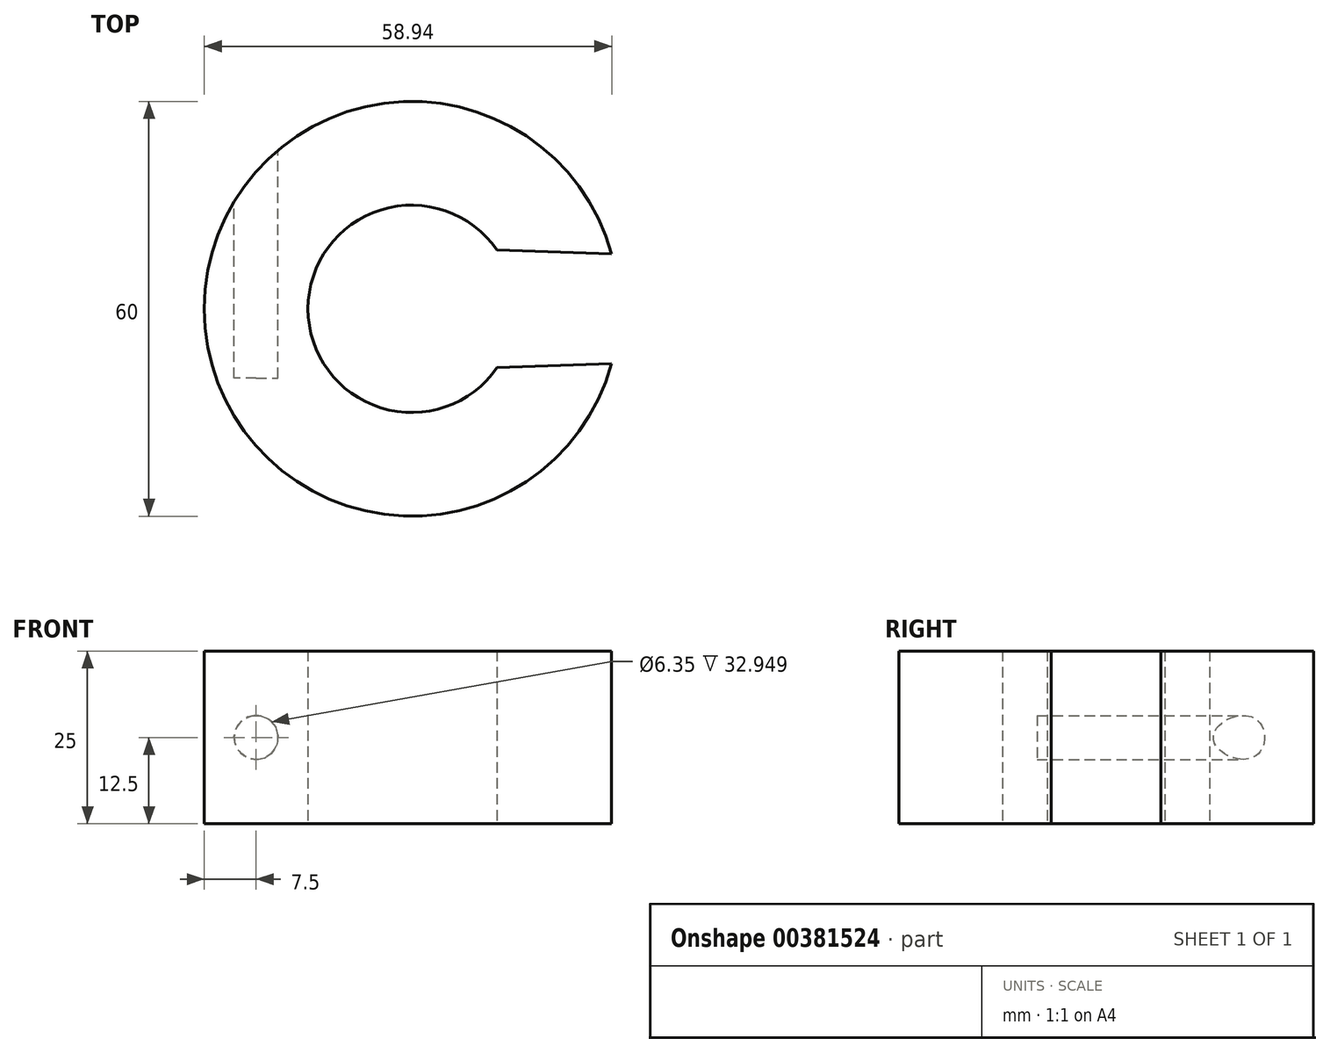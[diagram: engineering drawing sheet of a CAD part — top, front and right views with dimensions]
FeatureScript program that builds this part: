
annotation { "Feature Type Name" : "Feature", "Feature Type Description" : "" }
export const myFeature = defineFeature(function(context is Context, id is Id, definition is map)
    precondition{}
    {
        {
            var Q0;
            Q0=qCreatedBy(makeId("Top.planeOp"),FACE);
            var sketch = newSketch(context, id + "F0", { "sketchPlane" : qUnion([Q0])});
            skArc(sketch, "E0", {"start": v(12.36, 8.5) * mm, "mid": v(-15, 0) * mm, "end": v(12.36, -8.5) * mm});
            skArc(sketch, "E1.0", {"start": v(28.94, 7.92) * mm, "mid": v(-30, 0) * mm, "end": v(28.94, -7.92) * mm});
            skLineSegment(sketch, "E2", {"start": v(12.36, -8.5) * mm, "end": v(28.94, -7.92) * mm});
            skLineSegment(sketch, "E3", {"start": v(12.36, 8.5) * mm, "end": v(28.94, 7.92) * mm});
            skLineSegment(sketch, "E4", {"start": v(12.36, 8.5) * mm, "end": v(12.36, -8.5) * mm, "construction": true});
            skPoint(sketch, "E5", {"position": v(12.36, 0) * mm});
            skSolve(sketch);
        }
        {
            var Q0;
            Q0=makeQuery(id+"F0.imprint","IMPRINT",FACE,{"disambiguationData":[TD([[makeQuery(id+"F0.imprint","IMPRINT",EDGE,{"derivedFrom":sQuery(id+"F0.wireOp",EDGE,"E0")}),-1.0]])]});
            extrude(context, id + "F1", {"entities" : qUnion([Q0]), "depth" : 25 * mm});
        }
        {
            var Q0;
            Q0=qCreatedBy(makeId("Front.planeOp"),FACE);
            var sketch = newSketch(context, id + "F2", { "sketchPlane" : qUnion([Q0])});
            skCircle(sketch, "E6", {"center": v(-22.5, 12.5) * mm, "radius": 3.17 * mm});
            skPoint(sketch, "E7.0", {"position": v(-15, 25) * mm});
            skPoint(sketch, "E7.1", {"position": v(-30, 25) * mm});
            skLineSegment(sketch, "E8", {"start": v(-30, 25) * mm, "end": v(-15, 25) * mm, "construction": true});
            skPoint(sketch, "E9", {"position": v(-22.5, 25) * mm});
            skPoint(sketch, "E10.0", {"position": v(-30, 0) * mm});
            skPoint(sketch, "E10.1", {"position": v(-15, 0) * mm});
            skLineSegment(sketch, "E11", {"start": v(-30, 0) * mm, "end": v(-15, 0) * mm, "construction": true});
            skPoint(sketch, "E12", {"position": v(-22.5, 0) * mm});
            skLineSegment(sketch, "E13", {"start": v(-22.5, 0) * mm, "end": v(-22.5, 25) * mm, "construction": true});
            skSolve(sketch);
        }
        {
            var Q0;
            Q0 = qSketchRegion(id + "F2", true);
            extrude(context, id + "F3", {"entities" : qUnion([Q0]), "operationType" : NewBodyOperationType.REMOVE, "depth" : 10 * mm, "hasSecondDirection" : true, "secondDirectionBound" : SecondDirectionBoundingType.THROUGH_ALL, "secondDirectionOppositeDirection" : true, "secondDirectionDepth" : 25 * mm});
        }
    });
